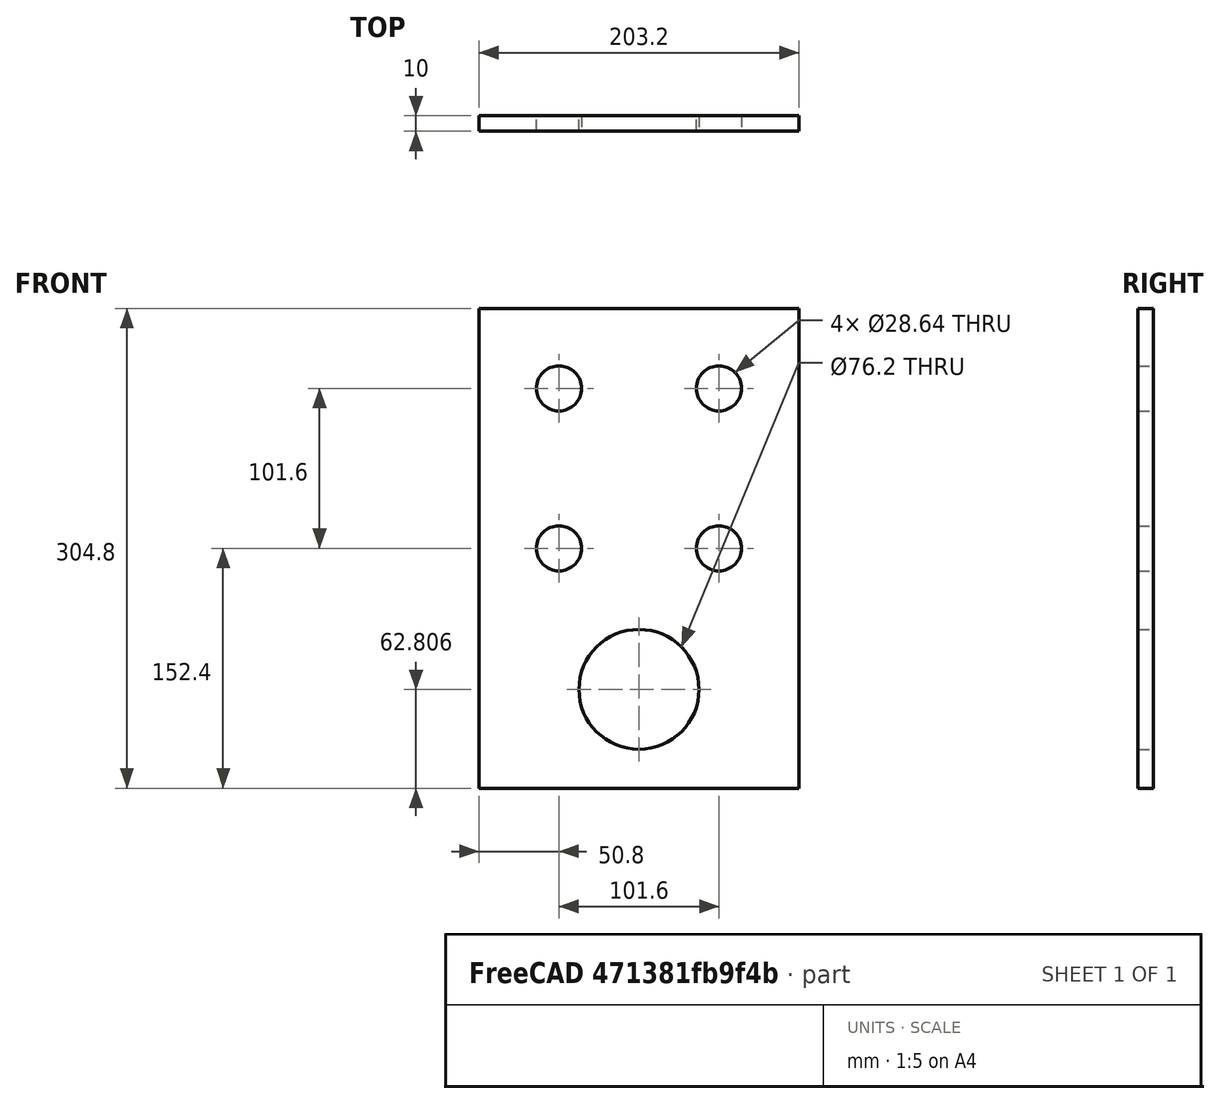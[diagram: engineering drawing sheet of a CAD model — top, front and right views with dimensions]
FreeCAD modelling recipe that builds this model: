
FCSTD DOCUMENT  (FreeCAD 0.16R6668 (Git))
Label: idler mount plate
License: All rights reserved
LicenseURL: http://en.wikipedia.org/wiki/All_rights_reserved
objects: Sketcher::SketchObject×1, PartDesign::Pad×1
note: 3 computed .brp shape members not serialized (recipe doc carries the construction recipe); baked Part::Feature solids carry a one-line shape summary decoded from their .brp

FEATURE [Sketcher::SketchObject] Sketch
  Placement = pos=(0,0,0) rot=(-1,0,0;4.71239rad)
  sketch-geometry (9):
    g0: LineSegment StartX=-101.6 StartY=152.4 StartZ=0 EndX=101.6 EndY=152.4 EndZ=0
    g1: LineSegment StartX=101.6 StartY=152.4 StartZ=0 EndX=101.6 EndY=-152.4 EndZ=0
    g2: LineSegment StartX=101.6 StartY=-152.4 StartZ=0 EndX=-101.6 EndY=-152.4 EndZ=0
    g3: LineSegment StartX=-101.6 StartY=-152.4 StartZ=0 EndX=-101.6 EndY=152.4 EndZ=0
    g4: Circle CenterX=50.8 CenterY=101.6 CenterZ=0 NormalX=0 NormalY=0 NormalZ=1 Radius=14.3183
    g5: Circle CenterX=-50.8 CenterY=0 CenterZ=0 NormalX=0 NormalY=0 NormalZ=1 Radius=14.3183
    g6: Circle CenterX=50.8 CenterY=0 CenterZ=0 NormalX=0 NormalY=0 NormalZ=1 Radius=14.3183
    g7: Circle CenterX=0 CenterY=-89.5944 CenterZ=0 NormalX=0 NormalY=0 NormalZ=1 Radius=38.1
    g8: Circle CenterX=-50.8 CenterY=101.6 CenterZ=0 NormalX=0 NormalY=0 NormalZ=1 Radius=14.3183
  constraints (24):
    c: Coincident(g0,g1)
    c: Coincident(g1,g2)
    c: Coincident(g2,g3)
    c: Coincident(g3,g0)
    c: Horizontal(g0)
    c: Horizontal(g2)
    c: Vertical(g1)
    c: Vertical(g3)
    c: DistanceX(g2,g2) = 203.2
    c: DistanceY(g1,g1) = 304.8
    c: Equal(g4,g5)
    c: Radius(g7) = 38.1
    c: Equal(g1,g3)
    c: Equal(g0,g2)
    c: Equal(g4,g6)
    c: DistanceX(g4,g0) = 50.8
    c: DistanceX(g6,g1) = 50.8
    c: DistanceX(g2,g5) = 50.8
    c: DistanceY(g4,g0) = 50.8
    c: DistanceY(g1,g6) = 152.4
    c: DistanceY(g2,g5) = 152.4
    c: DistanceX(g7,g1) = 101.6
    c: DistanceY(g1,g7) = 62.8056
    c: Equal(g4,g8)
FEATURE [PartDesign::Pad] Pad
  Length = 10
  Length2 = 100
  Placement = pos=(0,0,0) rot=(-1,0,0;4.71239rad)
  Sketch = -> Sketch
  Type = 0
